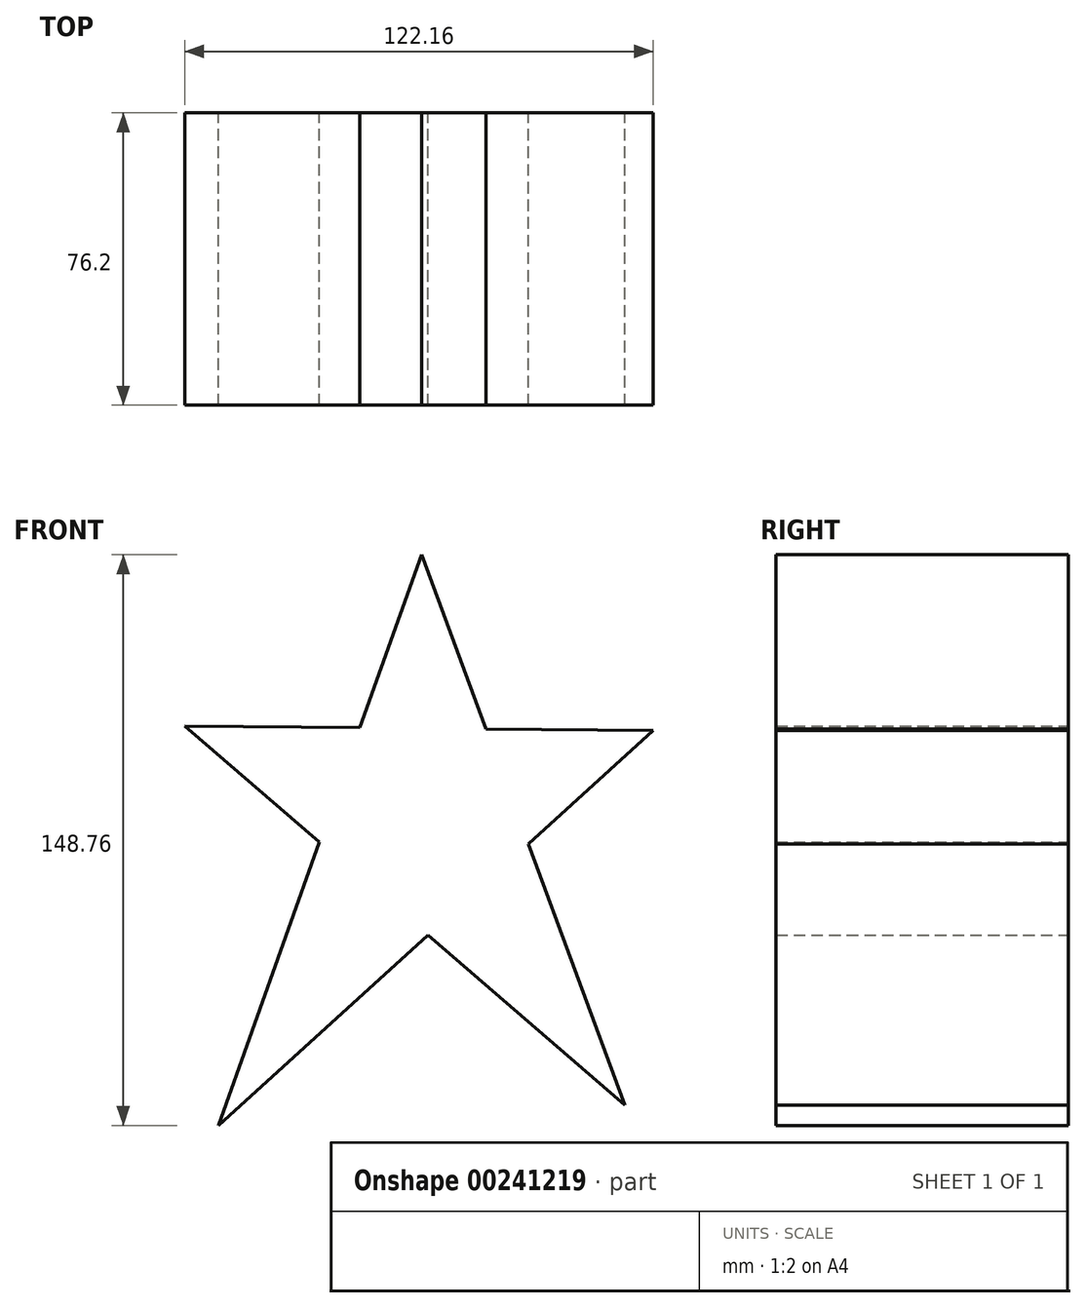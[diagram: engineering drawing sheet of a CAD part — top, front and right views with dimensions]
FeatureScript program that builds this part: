
annotation { "Feature Type Name" : "Feature", "Feature Type Description" : "" }
export const myFeature = defineFeature(function(context is Context, id is Id, definition is map)
    precondition{}
    {
        {
            var Q0;
            Q0=qCreatedBy(makeId("Front.planeOp"),FACE);
            var sketch = newSketch(context, id + "F0", { "sketchPlane" : qUnion([Q0])});
            skLineSegment(sketch, "E0", {"start": v(-52.97, -72.3) * mm, "end": v(60.43, 30.63) * mm});
            skLineSegment(sketch, "E1", {"start": v(58.32, 30.63) * mm, "end": v(60.43, 30.63) * mm});
            skLineSegment(sketch, "E2", {"start": v(60.43, 30.63) * mm, "end": v(-61.73, 31.82) * mm});
            skLineSegment(sketch, "E3", {"start": v(-61.73, 31.82) * mm, "end": v(53.07, -66.95) * mm});
            skLineSegment(sketch, "E4", {"start": v(53.07, -66.95) * mm, "end": v(0, 76.47) * mm});
            skLineSegment(sketch, "E5", {"start": v(0, 76.47) * mm, "end": v(-52.97, -72.3) * mm});
            skSolve(sketch);
        }
        {
            var Q0;
            {var subQ1=sQuery(id+"F0.wireOp",EDGE,"E0");var subQ5=sQuery(id+"F0.wireOp",EDGE,"E3");var subQ6=makeQuery(id+"F0.imprint","INTERSECT",VERTEX,{"derivedFrom":[subQ1,subQ5]});Q0=makeQuery(id+"F0.imprint","IMPRINT",FACE,{"disambiguationData":[TD([[makeQuery(id+"F0.imprint","IMPRINT",EDGE,{"disambiguationData":[TD([[subQ6,-1.0]])],"derivedFrom":subQ1}),1.0]])]});}
            var Q1;
            {var subQ0=sQuery(id+"F0.wireOp",EDGE,"E3");var subQ1=sQuery(id+"F0.wireOp",EDGE,"E2");var subQ2=makeQuery(id+"F0.imprint","INTERSECT",VERTEX,{"derivedFrom":[subQ1,subQ0]});Q1=makeQuery(id+"F0.imprint","IMPRINT",FACE,{"disambiguationData":[TD([[makeQuery(id+"F0.imprint","IMPRINT",EDGE,{"disambiguationData":[TD([[subQ2,1.0]])],"derivedFrom":subQ1}),1.0]])]});}
            var Q2;
            {var subQ0=sQuery(id+"F0.wireOp",EDGE,"E4");var subQ1=sQuery(id+"F0.wireOp",EDGE,"E2");var subQ2=makeQuery(id+"F0.imprint","INTERSECT",VERTEX,{"derivedFrom":[subQ1,subQ0]});Q2=makeQuery(id+"F0.imprint","IMPRINT",FACE,{"disambiguationData":[TD([[makeQuery(id+"F0.imprint","IMPRINT",EDGE,{"disambiguationData":[TD([[subQ2,-1.0]])],"derivedFrom":subQ1}),-1.0]])]});}
            var Q3;
            {var subQ0=sQuery(id+"F0.wireOp",EDGE,"E2");var subQ1=sQuery(id+"F0.wireOp",EDGE,"E0");var subQ2=makeQuery(id+"F0.imprint","INTERSECT",VERTEX,{"derivedFrom":[subQ1,subQ0]});Q3=makeQuery(id+"F0.imprint","IMPRINT",FACE,{"disambiguationData":[TD([[makeQuery(id+"F0.imprint","IMPRINT",EDGE,{"disambiguationData":[TD([[subQ2,1.0]])],"derivedFrom":subQ1}),1.0]])]});}
            var Q4;
            {var subQ0=sQuery(id+"F0.wireOp",EDGE,"E3");var subQ1=sQuery(id+"F0.wireOp",EDGE,"E0");var subQ2=makeQuery(id+"F0.imprint","INTERSECT",VERTEX,{"derivedFrom":[subQ1,subQ0]});Q4=makeQuery(id+"F0.imprint","IMPRINT",FACE,{"disambiguationData":[TD([[makeQuery(id+"F0.imprint","IMPRINT",EDGE,{"disambiguationData":[TD([[subQ2,-1.0]])],"derivedFrom":subQ1}),-1.0]])]});}
            var Q5;
            {var subQ0=sQuery(id+"F0.wireOp",EDGE,"E5");var subQ1=sQuery(id+"F0.wireOp",EDGE,"E0");var subQ2=makeQuery(id+"F0.imprint","INTERSECT",VERTEX,{"derivedFrom":[subQ1,subQ0]});Q5=makeQuery(id+"F0.imprint","IMPRINT",FACE,{"disambiguationData":[TD([[makeQuery(id+"F0.imprint","IMPRINT",EDGE,{"disambiguationData":[TD([[subQ2,-1.0]])],"derivedFrom":subQ1}),1.0]])]});}
            extrude(context, id + "F1", {"entities" : qUnion([Q0, Q1, Q2, Q3, Q4, Q5]), "depth" : 25.4 * mm});
        }
        {
            var Q0;
            Q0=makeQuery(id+"F1.opExtrude","CAP_FACE",FACE,{"disambiguationData":[OSD([sQuery(id+"F0.wireOp",EDGE,"E0"),sQuery(id+"F0.wireOp",EDGE,"E2"),sQuery(id+"F0.wireOp",EDGE,"E3"),sQuery(id+"F0.wireOp",EDGE,"E4"),sQuery(id+"F0.wireOp",EDGE,"E5")])],"isStart":false});
            extrude(context, id + "F2", {"entities" : qUnion([Q0]), "operationType" : NewBodyOperationType.ADD, "depth" : 25.4 * mm});
        }
        {
            var Q0;
            Q0=makeQuery(id+"F1.opExtrude","CAP_FACE",FACE,{"disambiguationData":[OSD([sQuery(id+"F0.wireOp",EDGE,"E0"),sQuery(id+"F0.wireOp",EDGE,"E2"),sQuery(id+"F0.wireOp",EDGE,"E3"),sQuery(id+"F0.wireOp",EDGE,"E4"),sQuery(id+"F0.wireOp",EDGE,"E5")])],"isStart":true});
            extrude(context, id + "F3", {"entities" : qUnion([Q0]), "operationType" : NewBodyOperationType.ADD, "depth" : 25.4 * mm});
        }
    });
